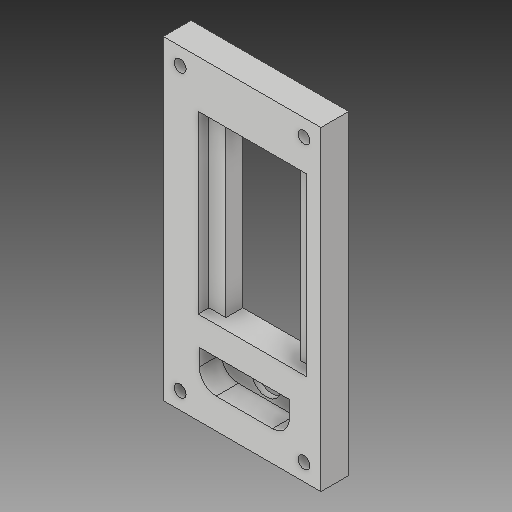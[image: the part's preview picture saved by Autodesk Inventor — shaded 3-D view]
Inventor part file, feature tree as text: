
AUTODESK INVENTOR PART (.ipt)
format: ipt  version: 2018 (Build 220112000, 112)  size: 176,128 bytes
history: native  units: in
note: dims shown in document units (in); Inventor stores cm internally (conversion verified against a paired STEP export)
features: sketch x4, extrude x4, plane x4, hole x4, fillet x1, projected_geometry x1
ambient origin geometry x8: Origin, YZ Plane, XZ Plane, XY Plane, X Axis, Y Axis, Z Axis, Center Point
bodies: Solid1 (feature_tree)
feature tree (18):
  sketch  "Sketch1"  dims[d0=3.5in d1=7.0in]
  extrude  "Extrusion1"  Depth=7.0in
  plane  "Work Plane1"
  plane  "Work Plane2"
  plane  "Work Plane3"
  plane  "Work Plane4"
  hole  "Hole2"  [1 undecoded]
  extrude  "Extrusion2"  Depth=1.65in
  sketch  "Sketch3"  dims[d4=1.65in d6=1.0496in]
  extrude  "Extrusion3"  Depth=3.9in
  extrude  "Extrusion4"  Depth=2.4in
  fillet  "Fillet1"  Radius=0.252in
  hole  "Hole5"  [1 undecoded]
  sketch  "Sketch2"  dims[d2=2.45in d3=3.9in]
  hole  "Hole1"  [1 undecoded]
  projected_geometry  "Projected Loop1"
  sketch  "Sketch5"  dims[d7=0.125in d8=0.0in d9=0.6562in d10=0.75in d11=0.375in d12=0.25in d13=0.5635in d14=1.0in d15=0.0in d16=3.9in d17=2.4in d18=0.252in d19=0.0in d20=1.0in d21=1.0in d22=0.75in d23=0.493in d24=0.0in d26=0.125in d27=0.493in d28=0.0in d29=0.024in d30=0.7126in d31=0.375in d39=0.266in d40=0.75in d41=0.375in d42=0.25in d43=0.5635in d44=1.0in d45=0.0in]
  hole  "Hole4"  [1 undecoded]
note: 4 required parameter values undecoded (feature->parameter linkage not recoverable at this tier; creation-order binding heuristic only, values carry confidence <= 0.55)
